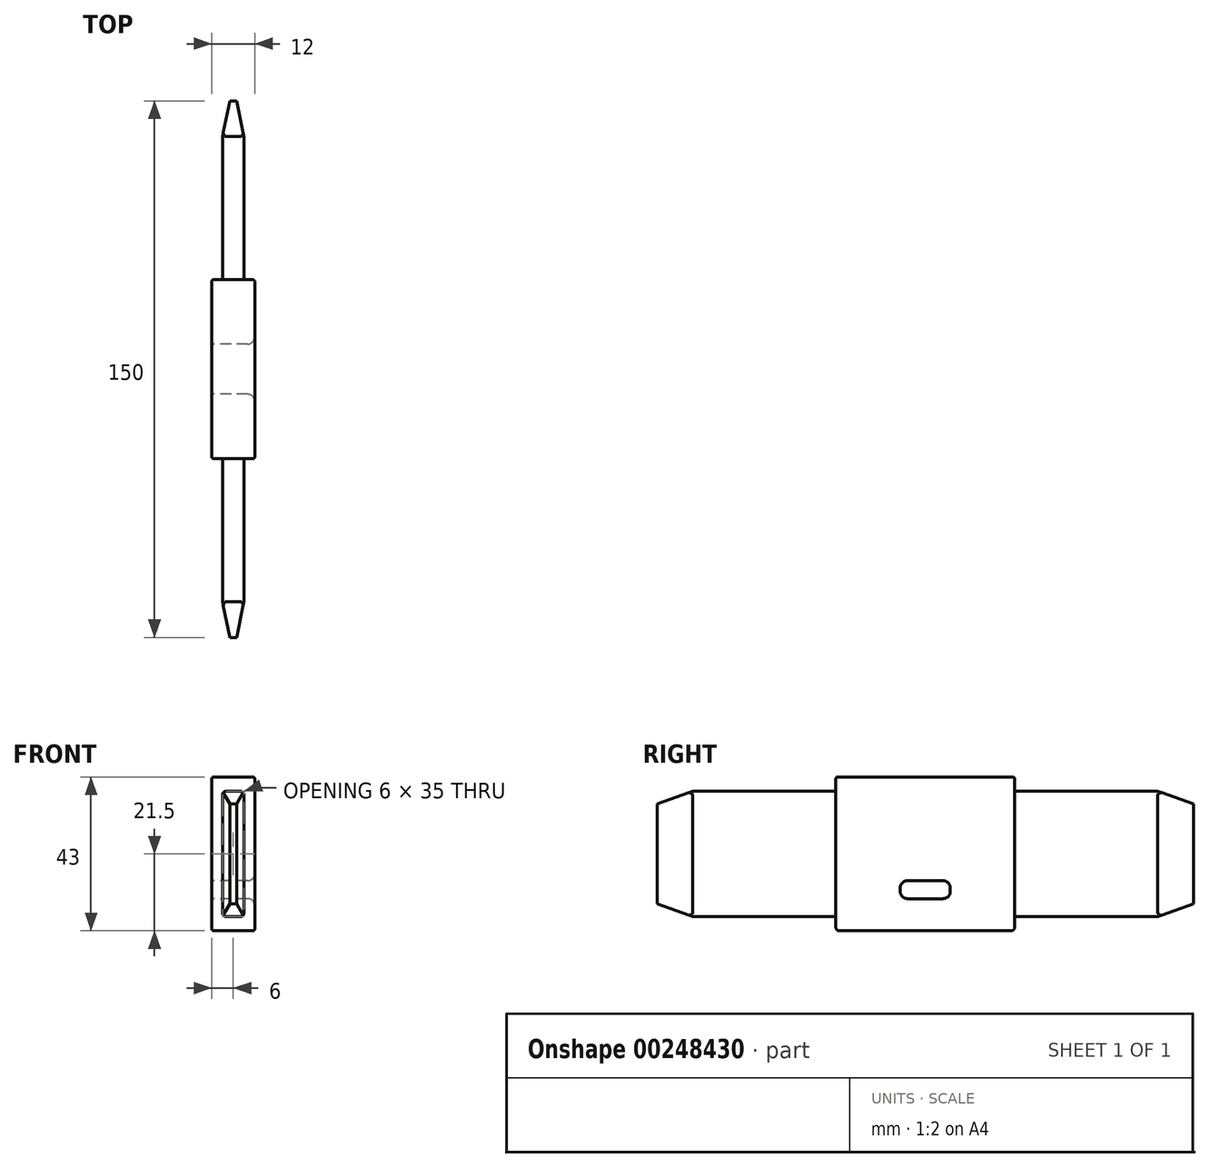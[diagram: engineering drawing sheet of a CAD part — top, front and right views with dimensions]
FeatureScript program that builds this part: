
annotation { "Feature Type Name" : "Feature", "Feature Type Description" : "" }
export const myFeature = defineFeature(function(context is Context, id is Id, definition is map)
    precondition{}
    {
        {
            var Q0;
            Q0=qCreatedBy(makeId("Right.planeOp"),FACE);
            var sketch = newSketch(context, id + "F0", { "sketchPlane" : qUnion([Q0])});
            skLineSegment(sketch, "E0.bottom", {"start": v(75, 17.5) * mm, "end": v(0, 17.5) * mm});
            skLineSegment(sketch, "E0.top", {"start": v(75, -17.5) * mm, "end": v(0, -17.5) * mm});
            skLineSegment(sketch, "E0.left", {"start": v(75, 17.5) * mm, "end": v(75, -17.5) * mm});
            skLineSegment(sketch, "E0.right", {"start": v(0, 17.5) * mm, "end": v(0, -17.5) * mm});
            skPoint(sketch, "E0.middle", {"position": v(37.5, 0) * mm});
            skSolve(sketch);
        }
        {
            var Q0;
            Q0 = qSketchRegion(id + "F0", true);
            extrude(context, id + "F1", {"entities" : qUnion([Q0]), "endBound" : BoundingType.SYMMETRIC, "depth" : 6 * mm, "offsetDistance" : 25 * mm});
        }
        {
            var Q0;
            Q0=makeQuery(id+"F1.opExtrude","SWEPT_FACE",FACE,{"disambiguationData":[OSD([sQuery(id+"F0.wireOp",EDGE,"E0.right")])]});
            var sketch = newSketch(context, id + "F2", { "sketchPlane" : qUnion([Q0])});
            skLineSegment(sketch, "E1.bottom", {"start": v(-1, 13.75) * mm, "end": v(1, 13.75) * mm});
            skLineSegment(sketch, "E1.top", {"start": v(-1, -13.75) * mm, "end": v(1, -13.75) * mm});
            skLineSegment(sketch, "E1.left", {"start": v(-1, 13.75) * mm, "end": v(-1, -13.75) * mm});
            skLineSegment(sketch, "E1.right", {"start": v(1, 13.75) * mm, "end": v(1, -13.75) * mm});
            skPoint(sketch, "E1.middle", {"position": v(0, 0) * mm});
            skSolve(sketch);
        }
        {
            var Q0;
            Q0=makeQuery(id+"F2.imprint","IMPRINT",FACE,{"disambiguationData":[TD([[makeQuery(id+"F2.imprint","IMPRINT",EDGE,{"derivedFrom":sQuery(id+"F2.wireOp",EDGE,"E1.bottom")}),1.0]])]});
            cPlane(context, id + "F3", {"entities" : qUnion([Q0]), "cplaneType" : CPlaneType.OFFSET, "offset" : 10 * mm, "oppositeDirection" : true, "width" : 150 * mm, "height" : 150 * mm});
        }
        {
            var Q0;
            Q0=qCreatedBy(id+"F3.planeOp",FACE);
            var sketch = newSketch(context, id + "F4", { "sketchPlane" : qUnion([Q0])});
            skLineSegment(sketch, "E2.bottom", {"start": v(-5.36, 17.5) * mm, "end": v(5.36, 17.5) * mm});
            skLineSegment(sketch, "E2.top", {"start": v(-5.36, -17.5) * mm, "end": v(5.36, -17.5) * mm});
            skLineSegment(sketch, "E2.left", {"start": v(-5.36, 17.5) * mm, "end": v(-5.36, -17.5) * mm});
            skLineSegment(sketch, "E2.right", {"start": v(5.36, 17.5) * mm, "end": v(5.36, -17.5) * mm});
            skPoint(sketch, "E2.middle", {"position": v(0, 0) * mm});
            skSolve(sketch);
        }
        {
            var Q0;
            Q0 = qSketchRegion(id + "F4", true);
            extrude(context, id + "F5", {"entities" : qUnion([Q0]), "operationType" : NewBodyOperationType.REMOVE, "depth" : 25 * mm});
        }
        {
            var Q1;
            Q1=makeQuery(id+"F6w6HKWlVUeMEL2_1.boolean.opBoolean","MERGE",FACE,{"derivedFrom":[makeQuery(id+"FQnCMFi02ZcKkRw_1.boolean.opBoolean","MERGE",FACE,{"derivedFrom":[makeQuery(id+"F5.boolean.opBoolean","COPY",FACE,{"derivedFrom":makeQuery(id+"F5.opExtrude","CAP_FACE",FACE,{"disambiguationData":[OSD([sQuery(id+"F4.wireOp",EDGE,"E2.bottom"),sQuery(id+"F4.wireOp",EDGE,"E2.top"),sQuery(id+"F4.wireOp",EDGE,"E2.left"),sQuery(id+"F4.wireOp",EDGE,"E2.right")])],"isStart":true})}),makeQuery(id+"FQnCMFi02ZcKkRw_1.opExtrude","SWEPT_FACE",FACE,{"disambiguationData":[OSD([sQuery(id+"FCKkJjlNEHkGwO5_1.wireOp",EDGE,"jdwdB2yL-CdGN-uq70-LQhb-J9qsBf9VZhnu.bottom")])]})]}),makeQuery(id+"F6w6HKWlVUeMEL2_1.opExtrude","SWEPT_FACE",FACE,{"disambiguationData":[OSD([sQuery(id+"FENI3cwNbEPP9a6_1.wireOp",EDGE,"WIIhECSp-WKJI-63DX-bFf7-gCpTdTVL9LAZ.bottom")])]})]});
            var Q2;
            Q2=makeQuery(id+"F2.imprint","IMPRINT",FACE,{"disambiguationData":[TD([[makeQuery(id+"F2.imprint","IMPRINT",EDGE,{"derivedFrom":sQuery(id+"F2.wireOp",EDGE,"E1.bottom")}),-1.0]])]});
            loft(context, id + "F6", {"operationType" : NewBodyOperationType.ADD, "sheetProfilesArray" : [{ "sheetProfileEntities" : qUnion([Q1]) }, { "sheetProfileEntities" : qUnion([Q2]) }]});
        }
        {
            var Q0;
            Q0=makeQuery(id+"F1.opExtrude","SWEPT_FACE",FACE,{"disambiguationData":[OSD([sQuery(id+"F0.wireOp",EDGE,"E0.left")])]});
            var sketch = newSketch(context, id + "F7", { "sketchPlane" : qUnion([Q0])});
            skLineSegment(sketch, "E3.bottom", {"start": v(1, 14) * mm, "end": v(-1, 14) * mm});
            skLineSegment(sketch, "E3.top", {"start": v(1, -14) * mm, "end": v(-1, -14) * mm});
            skLineSegment(sketch, "E3.left", {"start": v(1, 14) * mm, "end": v(1, -14) * mm});
            skLineSegment(sketch, "E3.right", {"start": v(-1, 14) * mm, "end": v(-1, -14) * mm});
            skPoint(sketch, "E3.middle", {"position": v(0, 0) * mm});
            skSolve(sketch);
        }
        {
            var Q0;
            Q0=makeQuery(id+"F7.imprint","IMPRINT",FACE,{"disambiguationData":[TD([[makeQuery(id+"F7.imprint","IMPRINT",EDGE,{"derivedFrom":sQuery(id+"F7.wireOp",EDGE,"E3.bottom")}),-1.0]])]});
            extrude(context, id + "F8", {"entities" : qUnion([Q0]), "operationType" : NewBodyOperationType.REMOVE, "depth" : 10 * mm});
        }
        {
            var Q0;
            Q0=makeQuery(id+"F1.opExtrude","SWEPT_FACE",FACE,{"disambiguationData":[OSD([sQuery(id+"F0.wireOp",EDGE,"E0.left")])]});
            extrude(context, id + "F9", {"entities" : qUnion([Q0]), "operationType" : NewBodyOperationType.REMOVE, "oppositeDirection" : true, "depth" : 10 * mm});
        }
        {
            var Q0;
            Q0=makeQuery(id+"F9.boolean.opBoolean","COPY",FACE,{"derivedFrom":makeQuery(id+"F9.opExtrude","CAP_FACE",FACE,{"disambiguationData":[OSD([sQuery(id+"F0.wireOp",EDGE,"E0.left")])],"isStart":false})});
            cPlane(context, id + "F10", {"entities" : qUnion([Q0]), "cplaneType" : CPlaneType.OFFSET, "offset" : 10 * mm, "width" : 150 * mm, "height" : 150 * mm});
        }
        {
            var Q0;
            Q0=qCreatedBy(id+"F10.planeOp",FACE);
            var sketch = newSketch(context, id + "F11", { "sketchPlane" : qUnion([Q0])});
            skLineSegment(sketch, "E4.bottom", {"start": v(1, 14) * mm, "end": v(-1, 14) * mm});
            skLineSegment(sketch, "E4.top", {"start": v(1, -14) * mm, "end": v(-1, -14) * mm});
            skLineSegment(sketch, "E4.left", {"start": v(1, 14) * mm, "end": v(1, -14) * mm});
            skLineSegment(sketch, "E4.right", {"start": v(-1, 14) * mm, "end": v(-1, -14) * mm});
            skPoint(sketch, "E4.middle", {"position": v(0, 0) * mm});
            skSolve(sketch);
        }
        {
            var Q1;
            Q1=makeQuery(id+"F9.boolean.opBoolean","COPY",FACE,{"derivedFrom":makeQuery(id+"F9.opExtrude","CAP_FACE",FACE,{"disambiguationData":[OSD([sQuery(id+"F0.wireOp",EDGE,"E0.left")])],"isStart":false})});
            var Q2;
            Q2=makeQuery(id+"F11.imprint","IMPRINT",FACE,{"disambiguationData":[TD([[makeQuery(id+"F11.imprint","IMPRINT",EDGE,{"derivedFrom":sQuery(id+"F11.wireOp",EDGE,"E4.bottom")}),1.0]])]});
            loft(context, id + "F12", {"operationType" : NewBodyOperationType.ADD, "sheetProfilesArray" : [{ "sheetProfileEntities" : qUnion([Q1]) }, { "sheetProfileEntities" : qUnion([Q2]) }]});
        }
        {
            var Q0;
            Q0=qCreatedBy(makeId("Right.planeOp"),FACE);
            var sketch = newSketch(context, id + "F13", { "sketchPlane" : qUnion([Q0])});
            skLineSegment(sketch, "E5.top", {"start": v(0, 21.5) * mm, "end": v(-25, 21.5) * mm});
            skLineSegment(sketch, "E5.right", {"start": v(-25, 0) * mm, "end": v(-25, 21.5) * mm});
            skLineSegment(sketch, "E6.MirrorCS", {"start": v(25, 0) * mm, "end": v(25, 21.5) * mm});
            skLineSegment(sketch, "E7.MirrorCS", {"start": v(0, 21.5) * mm, "end": v(25, 21.5) * mm});
            skLineSegment(sketch, "E8.MirrorCS", {"start": v(25, 0) * mm, "end": v(25, -21.5) * mm});
            skLineSegment(sketch, "E9.MirrorCS", {"start": v(0, -21.5) * mm, "end": v(25, -21.5) * mm});
            skLineSegment(sketch, "E10.MirrorCS", {"start": v(0, -21.5) * mm, "end": v(-25, -21.5) * mm});
            skLineSegment(sketch, "E11.MirrorCS", {"start": v(-25, 0) * mm, "end": v(-25, -21.5) * mm});
            skSolve(sketch);
        }
        {
            var Q0;
            Q0 = qSketchRegion(id + "F13", true);
            extrude(context, id + "F14", {"entities" : qUnion([Q0]), "operationType" : NewBodyOperationType.ADD, "endBound" : BoundingType.SYMMETRIC, "depth" : 12 * mm, "offsetDistance" : 25 * mm});
        }
        {
            var Q0;
            Q0=makeQuery(id+"F14.opExtrude","CAP_FACE",FACE,{"disambiguationData":[OSD([sQuery(id+"F13.wireOp",EDGE,"E5.top"),sQuery(id+"F13.wireOp",EDGE,"E5.right"),sQuery(id+"F13.wireOp",EDGE,"E6.MirrorCS"),sQuery(id+"F13.wireOp",EDGE,"E7.MirrorCS"),sQuery(id+"F13.wireOp",EDGE,"E8.MirrorCS"),sQuery(id+"F13.wireOp",EDGE,"E9.MirrorCS"),sQuery(id+"F13.wireOp",EDGE,"E10.MirrorCS"),sQuery(id+"F13.wireOp",EDGE,"E11.MirrorCS")])],"isStart":true});
            var sketch = newSketch(context, id + "F15", { "sketchPlane" : qUnion([Q0])});
            skLineSegment(sketch, "E12.bottom", {"start": v(5, -12.5) * mm, "end": v(-5, -12.5) * mm});
            skLineSegment(sketch, "E12.top", {"start": v(5, -7.5) * mm, "end": v(-5, -7.5) * mm});
            skLineSegment(sketch, "E12.left", {"start": v(7, -10.5) * mm, "end": v(7, -9.5) * mm});
            skLineSegment(sketch, "E12.right", {"start": v(-7, -10.5) * mm, "end": v(-7, -9.5) * mm});
            skPoint(sketch, "E12.middle", {"position": v(0, -10) * mm});
            skPoint(sketch, "E13.visualSharp", {"position": v(-7, -7.5) * mm});
            skArc(sketch, "E13.filletArc", {"start": v(-5, -7.5) * mm, "mid": v(-6.41, -8.09) * mm, "end": v(-7, -9.5) * mm});
            skPoint(sketch, "E14.visualSharp", {"position": v(-7, -12.5) * mm});
            skArc(sketch, "E14.filletArc", {"start": v(-7, -10.5) * mm, "mid": v(-6.41, -11.91) * mm, "end": v(-5, -12.5) * mm});
            skPoint(sketch, "E15.visualSharp", {"position": v(7, -12.5) * mm});
            skArc(sketch, "E15.filletArc", {"start": v(5, -12.5) * mm, "mid": v(6.41, -11.91) * mm, "end": v(7, -10.5) * mm});
            skPoint(sketch, "E16.visualSharp", {"position": v(7, -7.5) * mm});
            skArc(sketch, "E16.filletArc", {"start": v(7, -9.5) * mm, "mid": v(6.41, -8.09) * mm, "end": v(5, -7.5) * mm});
            skSolve(sketch);
        }
        {
            var Q0;
            Q0 = qSketchRegion(id + "F15", true);
            extrude(context, id + "F16", {"entities" : qUnion([Q0]), "operationType" : NewBodyOperationType.REMOVE, "oppositeDirection" : true, "depth" : 25 * mm});
        }
        {
            var Q0;
            Q0=makeQuery(id+"F16.boolean.opBoolean","INTERSECT",EDGE,{"derivedFrom":[makeQuery(id+"F14.opExtrude","CAP_FACE",FACE,{"disambiguationData":[OSD([sQuery(id+"F13.wireOp",EDGE,"E5.top"),sQuery(id+"F13.wireOp",EDGE,"E5.right"),sQuery(id+"F13.wireOp",EDGE,"E6.MirrorCS"),sQuery(id+"F13.wireOp",EDGE,"E7.MirrorCS"),sQuery(id+"F13.wireOp",EDGE,"E8.MirrorCS"),sQuery(id+"F13.wireOp",EDGE,"E9.MirrorCS"),sQuery(id+"F13.wireOp",EDGE,"E10.MirrorCS"),sQuery(id+"F13.wireOp",EDGE,"E11.MirrorCS")])],"isStart":false}),makeQuery(id+"F16.opExtrude","SWEPT_FACE",FACE,{"disambiguationData":[OSD([sQuery(id+"F15.wireOp",EDGE,"E12.top")])]})]});
            var Q1;
            Q1=makeQuery(id+"F16.boolean.opBoolean","INTERSECT",EDGE,{"derivedFrom":[makeQuery(id+"F14.opExtrude","CAP_FACE",FACE,{"disambiguationData":[OSD([sQuery(id+"F13.wireOp",EDGE,"E5.top"),sQuery(id+"F13.wireOp",EDGE,"E5.right"),sQuery(id+"F13.wireOp",EDGE,"E6.MirrorCS"),sQuery(id+"F13.wireOp",EDGE,"E7.MirrorCS"),sQuery(id+"F13.wireOp",EDGE,"E8.MirrorCS"),sQuery(id+"F13.wireOp",EDGE,"E9.MirrorCS"),sQuery(id+"F13.wireOp",EDGE,"E10.MirrorCS"),sQuery(id+"F13.wireOp",EDGE,"E11.MirrorCS")])],"isStart":false}),makeQuery(id+"F16.opExtrude","SWEPT_FACE",FACE,{"disambiguationData":[OSD([sQuery(id+"F15.wireOp",EDGE,"E16.filletArc")])]})]});
            var Q2;
            Q2=makeQuery(id+"F16.boolean.opBoolean","INTERSECT",EDGE,{"derivedFrom":[makeQuery(id+"F14.opExtrude","CAP_FACE",FACE,{"disambiguationData":[OSD([sQuery(id+"F13.wireOp",EDGE,"E5.top"),sQuery(id+"F13.wireOp",EDGE,"E5.right"),sQuery(id+"F13.wireOp",EDGE,"E6.MirrorCS"),sQuery(id+"F13.wireOp",EDGE,"E7.MirrorCS"),sQuery(id+"F13.wireOp",EDGE,"E8.MirrorCS"),sQuery(id+"F13.wireOp",EDGE,"E9.MirrorCS"),sQuery(id+"F13.wireOp",EDGE,"E10.MirrorCS"),sQuery(id+"F13.wireOp",EDGE,"E11.MirrorCS")])],"isStart":false}),makeQuery(id+"F16.opExtrude","SWEPT_FACE",FACE,{"disambiguationData":[OSD([sQuery(id+"F15.wireOp",EDGE,"E12.left")])]})]});
            var Q3;
            Q3=makeQuery(id+"F16.boolean.opBoolean","INTERSECT",EDGE,{"derivedFrom":[makeQuery(id+"F14.opExtrude","CAP_FACE",FACE,{"disambiguationData":[OSD([sQuery(id+"F13.wireOp",EDGE,"E5.top"),sQuery(id+"F13.wireOp",EDGE,"E5.right"),sQuery(id+"F13.wireOp",EDGE,"E6.MirrorCS"),sQuery(id+"F13.wireOp",EDGE,"E7.MirrorCS"),sQuery(id+"F13.wireOp",EDGE,"E8.MirrorCS"),sQuery(id+"F13.wireOp",EDGE,"E9.MirrorCS"),sQuery(id+"F13.wireOp",EDGE,"E10.MirrorCS"),sQuery(id+"F13.wireOp",EDGE,"E11.MirrorCS")])],"isStart":false}),makeQuery(id+"F16.opExtrude","SWEPT_FACE",FACE,{"disambiguationData":[OSD([sQuery(id+"F15.wireOp",EDGE,"E15.filletArc")])]})]});
            var Q4;
            Q4=makeQuery(id+"F16.boolean.opBoolean","INTERSECT",EDGE,{"derivedFrom":[makeQuery(id+"F14.opExtrude","CAP_FACE",FACE,{"disambiguationData":[OSD([sQuery(id+"F13.wireOp",EDGE,"E5.top"),sQuery(id+"F13.wireOp",EDGE,"E5.right"),sQuery(id+"F13.wireOp",EDGE,"E6.MirrorCS"),sQuery(id+"F13.wireOp",EDGE,"E7.MirrorCS"),sQuery(id+"F13.wireOp",EDGE,"E8.MirrorCS"),sQuery(id+"F13.wireOp",EDGE,"E9.MirrorCS"),sQuery(id+"F13.wireOp",EDGE,"E10.MirrorCS"),sQuery(id+"F13.wireOp",EDGE,"E11.MirrorCS")])],"isStart":false}),makeQuery(id+"F16.opExtrude","SWEPT_FACE",FACE,{"disambiguationData":[OSD([sQuery(id+"F15.wireOp",EDGE,"E12.bottom")])]})]});
            var Q5;
            Q5=makeQuery(id+"F16.boolean.opBoolean","INTERSECT",EDGE,{"derivedFrom":[makeQuery(id+"F14.opExtrude","CAP_FACE",FACE,{"disambiguationData":[OSD([sQuery(id+"F13.wireOp",EDGE,"E5.top"),sQuery(id+"F13.wireOp",EDGE,"E5.right"),sQuery(id+"F13.wireOp",EDGE,"E6.MirrorCS"),sQuery(id+"F13.wireOp",EDGE,"E7.MirrorCS"),sQuery(id+"F13.wireOp",EDGE,"E8.MirrorCS"),sQuery(id+"F13.wireOp",EDGE,"E9.MirrorCS"),sQuery(id+"F13.wireOp",EDGE,"E10.MirrorCS"),sQuery(id+"F13.wireOp",EDGE,"E11.MirrorCS")])],"isStart":false}),makeQuery(id+"F16.opExtrude","SWEPT_FACE",FACE,{"disambiguationData":[OSD([sQuery(id+"F15.wireOp",EDGE,"E13.filletArc")])]})]});
            var Q6;
            Q6=makeQuery(id+"F16.boolean.opBoolean","INTERSECT",EDGE,{"derivedFrom":[makeQuery(id+"F14.opExtrude","CAP_FACE",FACE,{"disambiguationData":[OSD([sQuery(id+"F13.wireOp",EDGE,"E5.top"),sQuery(id+"F13.wireOp",EDGE,"E5.right"),sQuery(id+"F13.wireOp",EDGE,"E6.MirrorCS"),sQuery(id+"F13.wireOp",EDGE,"E7.MirrorCS"),sQuery(id+"F13.wireOp",EDGE,"E8.MirrorCS"),sQuery(id+"F13.wireOp",EDGE,"E9.MirrorCS"),sQuery(id+"F13.wireOp",EDGE,"E10.MirrorCS"),sQuery(id+"F13.wireOp",EDGE,"E11.MirrorCS")])],"isStart":false}),makeQuery(id+"F16.opExtrude","SWEPT_FACE",FACE,{"disambiguationData":[OSD([sQuery(id+"F15.wireOp",EDGE,"E12.right")])]})]});
            var Q7;
            Q7=makeQuery(id+"F16.boolean.opBoolean","INTERSECT",EDGE,{"derivedFrom":[makeQuery(id+"F14.opExtrude","CAP_FACE",FACE,{"disambiguationData":[OSD([sQuery(id+"F13.wireOp",EDGE,"E5.top"),sQuery(id+"F13.wireOp",EDGE,"E5.right"),sQuery(id+"F13.wireOp",EDGE,"E6.MirrorCS"),sQuery(id+"F13.wireOp",EDGE,"E7.MirrorCS"),sQuery(id+"F13.wireOp",EDGE,"E8.MirrorCS"),sQuery(id+"F13.wireOp",EDGE,"E9.MirrorCS"),sQuery(id+"F13.wireOp",EDGE,"E10.MirrorCS"),sQuery(id+"F13.wireOp",EDGE,"E11.MirrorCS")])],"isStart":false}),makeQuery(id+"F16.opExtrude","SWEPT_FACE",FACE,{"disambiguationData":[OSD([sQuery(id+"F15.wireOp",EDGE,"E14.filletArc")])]})]});
            var Q8;
            Q8=makeQuery(id+"F16.boolean.opBoolean","COPY",EDGE,{"derivedFrom":makeQuery(id+"F16.opExtrude","CAP_EDGE",EDGE,{"disambiguationData":[OSD([sQuery(id+"F15.wireOp",EDGE,"E12.top")])],"isStart":true})});
            var Q9;
            Q9=makeQuery(id+"F16.boolean.opBoolean","COPY",EDGE,{"derivedFrom":makeQuery(id+"F16.opExtrude","CAP_EDGE",EDGE,{"disambiguationData":[OSD([sQuery(id+"F15.wireOp",EDGE,"E16.filletArc")])],"isStart":true})});
            var Q10;
            Q10=makeQuery(id+"F16.boolean.opBoolean","COPY",EDGE,{"derivedFrom":makeQuery(id+"F16.opExtrude","CAP_EDGE",EDGE,{"disambiguationData":[OSD([sQuery(id+"F15.wireOp",EDGE,"E12.left")])],"isStart":true})});
            var Q11;
            Q11=makeQuery(id+"F16.boolean.opBoolean","COPY",EDGE,{"derivedFrom":makeQuery(id+"F16.opExtrude","CAP_EDGE",EDGE,{"disambiguationData":[OSD([sQuery(id+"F15.wireOp",EDGE,"E15.filletArc")])],"isStart":true})});
            var Q12;
            Q12=makeQuery(id+"F16.boolean.opBoolean","COPY",EDGE,{"derivedFrom":makeQuery(id+"F16.opExtrude","CAP_EDGE",EDGE,{"disambiguationData":[OSD([sQuery(id+"F15.wireOp",EDGE,"E12.bottom")])],"isStart":true})});
            var Q13;
            Q13=makeQuery(id+"F16.boolean.opBoolean","COPY",EDGE,{"derivedFrom":makeQuery(id+"F16.opExtrude","CAP_EDGE",EDGE,{"disambiguationData":[OSD([sQuery(id+"F15.wireOp",EDGE,"E14.filletArc")])],"isStart":true})});
            var Q14;
            Q14=makeQuery(id+"F16.boolean.opBoolean","COPY",EDGE,{"derivedFrom":makeQuery(id+"F16.opExtrude","CAP_EDGE",EDGE,{"disambiguationData":[OSD([sQuery(id+"F15.wireOp",EDGE,"E12.right")])],"isStart":true})});
            var Q15;
            Q15=makeQuery(id+"F16.boolean.opBoolean","COPY",EDGE,{"derivedFrom":makeQuery(id+"F16.opExtrude","CAP_EDGE",EDGE,{"disambiguationData":[OSD([sQuery(id+"F15.wireOp",EDGE,"E13.filletArc")])],"isStart":true})});
            fillet(context, id + "F17", {"entities" : qUnion([Q0, Q1, Q2, Q3, Q4, Q5, Q6, Q7, Q8, Q9, Q10, Q11, Q12, Q13, Q14, Q15]), "radius" : 2 * mm, "tangentPropagation" : true, "allowEdgeOverflow" : false});
        }
        {
            var Q0;
            Q0=makeQuery(id+"F14.opExtrude","SWEPT_FACE",FACE,{"disambiguationData":[OSD([sQuery(id+"F13.wireOp",EDGE,"E5.top"),sQuery(id+"F13.wireOp",EDGE,"E7.MirrorCS")])]});
            var Q1;
            Q1=makeQuery(id+"F14.opExtrude","CAP_FACE",FACE,{"disambiguationData":[OSD([sQuery(id+"F13.wireOp",EDGE,"E5.top"),sQuery(id+"F13.wireOp",EDGE,"E5.right"),sQuery(id+"F13.wireOp",EDGE,"E6.MirrorCS"),sQuery(id+"F13.wireOp",EDGE,"E7.MirrorCS"),sQuery(id+"F13.wireOp",EDGE,"E8.MirrorCS"),sQuery(id+"F13.wireOp",EDGE,"E9.MirrorCS"),sQuery(id+"F13.wireOp",EDGE,"E10.MirrorCS"),sQuery(id+"F13.wireOp",EDGE,"E11.MirrorCS")])],"isStart":false});
            var Q2;
            Q2=makeQuery(id+"F14.opExtrude","CAP_FACE",FACE,{"disambiguationData":[OSD([sQuery(id+"F13.wireOp",EDGE,"E5.top"),sQuery(id+"F13.wireOp",EDGE,"E5.right"),sQuery(id+"F13.wireOp",EDGE,"E6.MirrorCS"),sQuery(id+"F13.wireOp",EDGE,"E7.MirrorCS"),sQuery(id+"F13.wireOp",EDGE,"E8.MirrorCS"),sQuery(id+"F13.wireOp",EDGE,"E9.MirrorCS"),sQuery(id+"F13.wireOp",EDGE,"E10.MirrorCS"),sQuery(id+"F13.wireOp",EDGE,"E11.MirrorCS")])],"isStart":true});
            fillet(context, id + "F18", {"entities" : qUnion([Q0, Q1, Q2]), "radius" : 0.5 * mm, "tangentPropagation" : true, "allowEdgeOverflow" : false});
        }
        {
            var Q0;
            Q0=makeQuery(id+"F1.opExtrude","SWEPT_BODY",BODY,{"disambiguationData":[OSD([sQuery(id+"F0.wireOp",EDGE,"E0.bottom"),sQuery(id+"F0.wireOp",EDGE,"E0.top"),sQuery(id+"F0.wireOp",EDGE,"E0.left"),sQuery(id+"F0.wireOp",EDGE,"E0.right")])]});
            var Q1;
            Q1=makeQuery(id+"FOujzRG0Ec1wnBN_1.opExtrude","SWEPT_BODY",BODY,{"disambiguationData":[OSD([sQuery(id+"FrSDGNufU6ULj9j_1.wireOp",EDGE,"IVTF4n7o-aijf-8SLD-BCab-RpEN54KbcJAq")])]});
            var Q2;
            Q2=qCreatedBy(makeId("Front.planeOp"),FACE);
            mirror(context, id + "F19", {"operationType" : NewBodyOperationType.ADD, "entities" : qUnion([Q0, Q1]), "mirrorPlane" : qUnion([Q2])});
        }
        {
            var Q0;
            Q0=makeQuery(id+"F14.opExtrude","SWEPT_EDGE",EDGE,{"disambiguationData":[OSD([sQuery(id+"F13.wireOp",EDGE,"E8.MirrorCS"),sQuery(id+"F13.wireOp",EDGE,"E9.MirrorCS")])]});
            var Q1;
            Q1=makeQuery(id+"F14.opExtrude","SWEPT_EDGE",EDGE,{"disambiguationData":[OSD([sQuery(id+"F13.wireOp",EDGE,"E10.MirrorCS"),sQuery(id+"F13.wireOp",EDGE,"E11.MirrorCS")])]});
            fillet(context, id + "F20", {"entities" : qUnion([Q0, Q1]), "radius" : 1 * mm, "tangentPropagation" : true, "allowEdgeOverflow" : false});
        }
        {
            var Q0;
            Q0=makeQuery(id+"F1.opExtrude","CAP_EDGE",EDGE,{"disambiguationData":[OSD([sQuery(id+"F0.wireOp",EDGE,"E0.top")])],"isStart":false});
            var Q1;
            Q1=makeQuery(id+"F1.opExtrude","CAP_EDGE",EDGE,{"disambiguationData":[OSD([sQuery(id+"F0.wireOp",EDGE,"E0.bottom")])],"isStart":false});
            var Q2;
            Q2=makeQuery(id+"F1.opExtrude","CAP_EDGE",EDGE,{"disambiguationData":[OSD([sQuery(id+"F0.wireOp",EDGE,"E0.bottom")])],"isStart":true});
            var Q3;
            Q3=makeQuery(id+"F1.opExtrude","CAP_EDGE",EDGE,{"disambiguationData":[OSD([sQuery(id+"F0.wireOp",EDGE,"E0.top")])],"isStart":true});
            var Q4;
            Q4=makeQuery(id+"F19.opPattern","COPY",EDGE,{"derivedFrom":makeQuery(id+"F1.opExtrude","CAP_EDGE",EDGE,{"disambiguationData":[OSD([sQuery(id+"F0.wireOp",EDGE,"E0.bottom")])],"isStart":true}),"instanceName":"1"});
            var Q5;
            Q5=makeQuery(id+"F19.opPattern","COPY",EDGE,{"derivedFrom":makeQuery(id+"F1.opExtrude","CAP_EDGE",EDGE,{"disambiguationData":[OSD([sQuery(id+"F0.wireOp",EDGE,"E0.top")])],"isStart":true}),"instanceName":"1"});
            var Q6;
            Q6=makeQuery(id+"F19.opPattern","COPY",EDGE,{"derivedFrom":makeQuery(id+"F1.opExtrude","CAP_EDGE",EDGE,{"disambiguationData":[OSD([sQuery(id+"F0.wireOp",EDGE,"E0.top")])],"isStart":false}),"instanceName":"1"});
            var Q7;
            Q7=makeQuery(id+"F19.opPattern","COPY",EDGE,{"derivedFrom":makeQuery(id+"F1.opExtrude","CAP_EDGE",EDGE,{"disambiguationData":[OSD([sQuery(id+"F0.wireOp",EDGE,"E0.bottom")])],"isStart":false}),"instanceName":"1"});
            fillet(context, id + "F21", {"entities" : qUnion([Q0, Q1, Q2, Q3, Q4, Q5, Q6, Q7]), "radius" : 1 * mm, "tangentPropagation" : true, "allowEdgeOverflow" : false});
        }
    });
